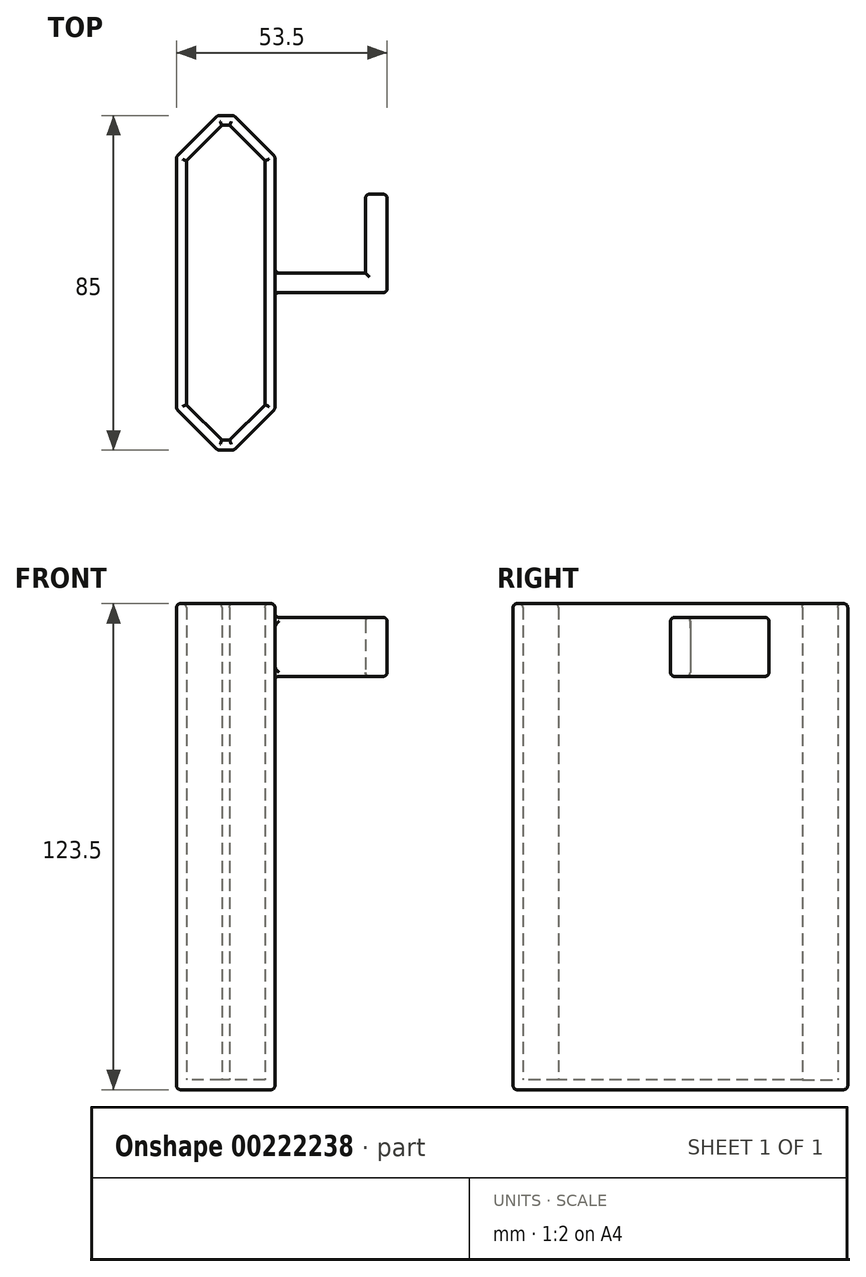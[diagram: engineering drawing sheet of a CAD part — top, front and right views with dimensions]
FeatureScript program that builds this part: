
annotation { "Feature Type Name" : "Feature", "Feature Type Description" : "" }
export const myFeature = defineFeature(function(context is Context, id is Id, definition is map)
    precondition{}
    {
        {
            var Q0;
            Q0=qCreatedBy(makeId("Top.planeOp"),FACE);
            var sketch = newSketch(context, id + "F0", { "sketchPlane" : qUnion([Q0])});
            skPoint(sketch, "E0.middle", {"position": v(0, 0) * mm});
            skPoint(sketch, "E1", {"position": v(-10, 31) * mm});
            skPoint(sketch, "E2", {"position": v(10, 31) * mm});
            skPoint(sketch, "E3", {"position": v(10, -31) * mm});
            skPoint(sketch, "E4", {"position": v(-10, -31) * mm});
            skPoint(sketch, "E5", {"position": v(-1, 40) * mm});
            skPoint(sketch, "E6", {"position": v(-1, -40) * mm});
            skPoint(sketch, "E7", {"position": v(1, 40) * mm});
            skPoint(sketch, "E8", {"position": v(1, -40) * mm});
            skLineSegment(sketch, "E9", {"start": v(1, 40) * mm, "end": v(-1, 40) * mm});
            skLineSegment(sketch, "E10", {"start": v(-1, 40) * mm, "end": v(-10, 31) * mm});
            skLineSegment(sketch, "E11", {"start": v(-10, 31) * mm, "end": v(-10, -31) * mm});
            skLineSegment(sketch, "E12", {"start": v(-10, -31) * mm, "end": v(-1, -40) * mm});
            skLineSegment(sketch, "E13", {"start": v(-1, -40) * mm, "end": v(1, -40) * mm});
            skLineSegment(sketch, "E14", {"start": v(1, -40) * mm, "end": v(10, -31) * mm});
            skLineSegment(sketch, "E15", {"start": v(10, -31) * mm, "end": v(10, 31) * mm});
            skLineSegment(sketch, "E16", {"start": v(10, 31) * mm, "end": v(1, 40) * mm});
            skLineSegment(sketch, "E17.0", {"start": v(12.5, 32.04) * mm, "end": v(2.04, 42.5) * mm});
            skLineSegment(sketch, "E17.1", {"start": v(12.5, -32.04) * mm, "end": v(12.5, 32.04) * mm});
            skLineSegment(sketch, "E17.2", {"start": v(2.04, 42.5) * mm, "end": v(-2.04, 42.5) * mm});
            skLineSegment(sketch, "E17.3", {"start": v(2.04, -42.5) * mm, "end": v(12.5, -32.04) * mm});
            skLineSegment(sketch, "E17.4", {"start": v(-2.04, 42.5) * mm, "end": v(-12.5, 32.04) * mm});
            skLineSegment(sketch, "E17.5", {"start": v(-12.5, 32.04) * mm, "end": v(-12.5, -32.04) * mm});
            skLineSegment(sketch, "E17.6", {"start": v(-12.5, -32.04) * mm, "end": v(-2.04, -42.5) * mm});
            skLineSegment(sketch, "E17.7", {"start": v(-2.04, -42.5) * mm, "end": v(2.04, -42.5) * mm});
            skSolve(sketch);
        }
        {
            var Q0;
            Q0=makeQuery(id+"F0.imprint","IMPRINT",FACE,{"disambiguationData":[TD([[makeQuery(id+"F0.imprint","IMPRINT",EDGE,{"derivedFrom":sQuery(id+"F0.wireOp",EDGE,"E9")}),1.0]])]});
            extrude(context, id + "F1", {"entities" : qUnion([Q0]), "depth" : 2.5 * mm, "offsetDistance" : 25 * mm});
        }
        {
            var Q0;
            Q0=makeQuery(id+"F0.imprint","IMPRINT",FACE,{"disambiguationData":[TD([[makeQuery(id+"F0.imprint","IMPRINT",EDGE,{"derivedFrom":sQuery(id+"F0.wireOp",EDGE,"E9")}),-1.0]])]});
            extrude(context, id + "F2", {"entities" : qUnion([Q0]), "operationType" : NewBodyOperationType.ADD, "depth" : 123.5 * mm, "offsetDistance" : 25 * mm});
        }
        {
            var Q0;
            Q0=makeQuery(id+"F2.opExtrude","SWEPT_FACE",FACE,{"disambiguationData":[OSD([sQuery(id+"F0.wireOp",EDGE,"E17.1")])]});
            var sketch = newSketch(context, id + "F3", { "sketchPlane" : qUnion([Q0])});
            skPoint(sketch, "E18", {"position": v(-2.5, 120) * mm});
            skPoint(sketch, "E19", {"position": v(-2.5, 105) * mm});
            skLineSegment(sketch, "E20.bottom", {"start": v(-2.5, 120) * mm, "end": v(2.5, 120) * mm});
            skLineSegment(sketch, "E20.top", {"start": v(-2.5, 105) * mm, "end": v(2.5, 105) * mm});
            skLineSegment(sketch, "E20.left", {"start": v(-2.5, 120) * mm, "end": v(-2.5, 105) * mm});
            skLineSegment(sketch, "E20.right", {"start": v(2.5, 120) * mm, "end": v(2.5, 105) * mm});
            skLineSegment(sketch, "E21.bottom", {"start": v(2.5, 120) * mm, "end": v(22.5, 120) * mm});
            skLineSegment(sketch, "E21.top", {"start": v(2.5, 105) * mm, "end": v(22.5, 105) * mm});
            skLineSegment(sketch, "E21.right", {"start": v(22.5, 120) * mm, "end": v(22.5, 105) * mm});
            skSolve(sketch);
        }
        {
            var Q0;
            Q0=makeQuery(id+"F3.imprint","IMPRINT",FACE,{"disambiguationData":[TD([[makeQuery(id+"F3.imprint","IMPRINT",EDGE,{"derivedFrom":sQuery(id+"F3.wireOp",EDGE,"E20.bottom")}),-1.0]])]});
            extrude(context, id + "F4", {"entities" : qUnion([Q0]), "operationType" : NewBodyOperationType.ADD, "depth" : 28.5 * mm, "offsetDistance" : 25 * mm});
        }
        {
            var Q0;
            Q0=makeQuery(id+"F3.imprint","IMPRINT",FACE,{"disambiguationData":[TD([[makeQuery(id+"F3.imprint","IMPRINT",EDGE,{"derivedFrom":sQuery(id+"F3.wireOp",EDGE,"E21.bottom")}),-1.0]])]});
            extrude(context, id + "F5", {"entities" : qUnion([Q0]), "operationType" : NewBodyOperationType.ADD, "depth" : 28.5 * mm, "offsetDistance" : 25 * mm, "hasSecondDirection" : true, "secondDirectionOppositeDirection" : false, "secondDirectionDepth" : 23 * mm});
        }
        {
            var Q0;
            Q0=makeQuery(id+"F2.opExtrude","CAP_FACE",FACE,{"disambiguationData":[OSD([sQuery(id+"F0.wireOp",EDGE,"E9"),sQuery(id+"F0.wireOp",EDGE,"E10"),sQuery(id+"F0.wireOp",EDGE,"E11"),sQuery(id+"F0.wireOp",EDGE,"E12"),sQuery(id+"F0.wireOp",EDGE,"E13"),sQuery(id+"F0.wireOp",EDGE,"E14"),sQuery(id+"F0.wireOp",EDGE,"E15"),sQuery(id+"F0.wireOp",EDGE,"E16"),sQuery(id+"F0.wireOp",EDGE,"E17.0"),sQuery(id+"F0.wireOp",EDGE,"E17.1"),sQuery(id+"F0.wireOp",EDGE,"E17.2"),sQuery(id+"F0.wireOp",EDGE,"E17.3"),sQuery(id+"F0.wireOp",EDGE,"E17.4"),sQuery(id+"F0.wireOp",EDGE,"E17.5"),sQuery(id+"F0.wireOp",EDGE,"E17.6"),sQuery(id+"F0.wireOp",EDGE,"E17.7")])],"isStart":false});
            var Q1;
            Q1=makeQuery(id+"F5.boolean.opBoolean","MERGE",FACE,{"derivedFrom":[makeQuery(id+"F4.opExtrude","SWEPT_FACE",FACE,{"disambiguationData":[OSD([sQuery(id+"F3.wireOp",EDGE,"E20.bottom")])]}),makeQuery(id+"F5.opExtrude","SWEPT_FACE",FACE,{"disambiguationData":[OSD([sQuery(id+"F3.wireOp",EDGE,"E21.bottom")])]})]});
            var Q2;
            Q2=makeQuery(id+"F5.boolean.opBoolean","MERGE",FACE,{"derivedFrom":[makeQuery(id+"F4.opExtrude","SWEPT_FACE",FACE,{"disambiguationData":[OSD([sQuery(id+"F3.wireOp",EDGE,"E20.top")])]}),makeQuery(id+"F5.opExtrude","SWEPT_FACE",FACE,{"disambiguationData":[OSD([sQuery(id+"F3.wireOp",EDGE,"E21.top")])]})]});
            var Q3;
            {var subQ0=sQuery(id+"F0.wireOp",EDGE,"E16");var subQ1=sQuery(id+"F0.wireOp",EDGE,"E15");var subQ2=sQuery(id+"F0.wireOp",EDGE,"E14");var subQ3=sQuery(id+"F0.wireOp",EDGE,"E13");var subQ4=sQuery(id+"F0.wireOp",EDGE,"E12");var subQ5=sQuery(id+"F0.wireOp",EDGE,"E11");var subQ6=sQuery(id+"F0.wireOp",EDGE,"E10");var subQ7=sQuery(id+"F0.wireOp",EDGE,"E9");Q3=makeQuery(id+"F2.boolean.opBoolean","MERGE",FACE,{"derivedFrom":[makeQuery(id+"F1.opExtrude","CAP_FACE",FACE,{"disambiguationData":[OSD([subQ7,subQ6,subQ5,subQ4,subQ3,subQ2,subQ1,subQ0])],"isStart":true}),makeQuery(id+"F2.opExtrude","CAP_FACE",FACE,{"disambiguationData":[OSD([subQ7,subQ6,subQ5,subQ4,subQ3,subQ2,subQ1,subQ0,sQuery(id+"F0.wireOp",EDGE,"E17.0"),sQuery(id+"F0.wireOp",EDGE,"E17.1"),sQuery(id+"F0.wireOp",EDGE,"E17.2"),sQuery(id+"F0.wireOp",EDGE,"E17.3"),sQuery(id+"F0.wireOp",EDGE,"E17.4"),sQuery(id+"F0.wireOp",EDGE,"E17.5"),sQuery(id+"F0.wireOp",EDGE,"E17.6"),sQuery(id+"F0.wireOp",EDGE,"E17.7")])],"isStart":true})]});}
            var Q4;
            Q4=makeQuery(id+"F2.opExtrude","SWEPT_EDGE",EDGE,{"disambiguationData":[OSD([sQuery(id+"F0.wireOp",EDGE,"E17.2"),sQuery(id+"F0.wireOp",EDGE,"E17.4")])]});
            var Q5;
            Q5=makeQuery(id+"F2.opExtrude","SWEPT_EDGE",EDGE,{"disambiguationData":[OSD([sQuery(id+"F0.wireOp",EDGE,"E17.4"),sQuery(id+"F0.wireOp",EDGE,"E17.5")])]});
            var Q6;
            Q6=makeQuery(id+"F2.opExtrude","SWEPT_EDGE",EDGE,{"disambiguationData":[OSD([sQuery(id+"F0.wireOp",EDGE,"E17.5"),sQuery(id+"F0.wireOp",EDGE,"E17.6")])]});
            var Q7;
            Q7=makeQuery(id+"F2.opExtrude","SWEPT_EDGE",EDGE,{"disambiguationData":[OSD([sQuery(id+"F0.wireOp",EDGE,"E17.6"),sQuery(id+"F0.wireOp",EDGE,"E17.7")])]});
            var Q8;
            Q8=makeQuery(id+"F2.opExtrude","SWEPT_EDGE",EDGE,{"disambiguationData":[OSD([sQuery(id+"F0.wireOp",EDGE,"E17.0"),sQuery(id+"F0.wireOp",EDGE,"E17.2")])]});
            var Q9;
            Q9=makeQuery(id+"F2.opExtrude","SWEPT_EDGE",EDGE,{"disambiguationData":[OSD([sQuery(id+"F0.wireOp",EDGE,"E17.0"),sQuery(id+"F0.wireOp",EDGE,"E17.1")])]});
            var Q10;
            Q10=makeQuery(id+"F2.opExtrude","SWEPT_EDGE",EDGE,{"disambiguationData":[OSD([sQuery(id+"F0.wireOp",EDGE,"E17.1"),sQuery(id+"F0.wireOp",EDGE,"E17.3")])]});
            var Q11;
            Q11=makeQuery(id+"F2.opExtrude","SWEPT_EDGE",EDGE,{"disambiguationData":[OSD([sQuery(id+"F0.wireOp",EDGE,"E17.3"),sQuery(id+"F0.wireOp",EDGE,"E17.7")])]});
            var Q12;
            Q12=makeQuery(id+"FO2EzPOl8wmNTCV_1.boolean.opBoolean","COPY",FACE,{"derivedFrom":makeQuery(id+"FO2EzPOl8wmNTCV_1.opExtrude","CAP_FACE",FACE,{"disambiguationData":[OSD([sQuery(id+"FU0Tr8krDVig9cX_1.wireOp",EDGE,"979xp39b-9xJF-zSxP-7RtF-dPhXLLhm7G3x.bottom"),sQuery(id+"FU0Tr8krDVig9cX_1.wireOp",EDGE,"979xp39b-9xJF-zSxP-7RtF-dPhXLLhm7G3x.top"),sQuery(id+"FU0Tr8krDVig9cX_1.wireOp",EDGE,"979xp39b-9xJF-zSxP-7RtF-dPhXLLhm7G3x.left"),sQuery(id+"FU0Tr8krDVig9cX_1.wireOp",EDGE,"979xp39b-9xJF-zSxP-7RtF-dPhXLLhm7G3x.right")])],"isStart":false})});
            var Q13;
            Q13=makeQuery(id+"FO2EzPOl8wmNTCV_1.boolean.opBoolean","INTERSECT",EDGE,{"derivedFrom":[makeQuery(id+"F1.opExtrude","CAP_FACE",FACE,{"disambiguationData":[OSD([sQuery(id+"F0.wireOp",EDGE,"E9"),sQuery(id+"F0.wireOp",EDGE,"E10"),sQuery(id+"F0.wireOp",EDGE,"E11"),sQuery(id+"F0.wireOp",EDGE,"E12"),sQuery(id+"F0.wireOp",EDGE,"E13"),sQuery(id+"F0.wireOp",EDGE,"E14"),sQuery(id+"F0.wireOp",EDGE,"E15"),sQuery(id+"F0.wireOp",EDGE,"E16")])],"isStart":false}),makeQuery(id+"FO2EzPOl8wmNTCV_1.opExtrude","SWEPT_FACE",FACE,{"disambiguationData":[OSD([sQuery(id+"FU0Tr8krDVig9cX_1.wireOp",EDGE,"979xp39b-9xJF-zSxP-7RtF-dPhXLLhm7G3x.right")])]})]});
            var Q14;
            Q14=makeQuery(id+"F5.opExtrude","SWEPT_FACE",FACE,{"disambiguationData":[OSD([sQuery(id+"F3.wireOp",EDGE,"E21.right")])]});
            var Q15;
            Q15=makeQuery(id+"F4.opExtrude","CAP_EDGE",EDGE,{"disambiguationData":[OSD([sQuery(id+"F3.wireOp",EDGE,"E20.left")])],"isStart":false});
            fillet(context, id + "F6", {"entities" : qUnion([Q0, Q1, Q2, Q3, Q4, Q5, Q6, Q7, Q8, Q9, Q10, Q11, Q12, Q13, Q14, Q15]), "radius" : 1 * mm, "tangentPropagation" : true, "allowEdgeOverflow" : false});
        }
    });
